# Revit family: Air_Handling_Unit-Package-Temperzone-OPA_171_211RLTFY
name_source: partatom
category: Mechanical Equipment
units: mm (PartAtom-declared; Revit-internal decimal feet)

## family parameters
Always vertical = Yes
Cut with Voids When Loaded = No
Maintain Annotation Orientation = No
OmniClass Number = 23.75.35.14
OmniClass Title = Air Handling Units
Part Type = Normal
Room Calculation Point = No
Round Connector Dimension = Use Radius
Shared = No
Work Plane-Based = No

## types (4) — shared parameters
Clearance Zones = Clearance Zones
ClearanceBack = 500 mm  [stored 1.64042 ft]
ClearanceLeft = 1000 mm  [stored 3.28084 ft]
ClearanceTop = 2000 mm
Condensate Drain = Condensate Drain - 1/2" BSP Female
CondensorFanBackOffset = 411 mm  [stored 1.34843 ft]
CondensorFanHeight = 18 mm  [stored 0.0590551 ft]
CondensorFanRadius = 290 mm  [stored 0.951444 ft]
Controller = UC8
DrainageBackOffset = 772 mm  [stored 2.53281 ft]
DrainageDia = 13 mm
DrainageLength = 30 mm  [stored 0.0984252 ft]
DrainageVerticalOffset = 83 mm  [stored 0.27231 ft]
ElectricInputVerticalOffset = 654 mm  [stored 2.14567 ft]
ElectricalRightOffset = 57 mm  [stored 0.187008 ft]
Finish = Grey Polyester Powder Coat
Indoor Fan Full Load Amps = 3 A/ph.
IndoorAirFanMotor = EC Motor
Manufacturer = temperzone ltd
ModifiedIssue_ANZRS = 250815.01 $
MountingFootHalfWidth = 64 mm
MountingFootLeftOffset = 24 mm  [stored 0.0787402 ft]
MountingPointLength = 800 mm  [stored 2.62467 ft]
NOTE = Models are representative of actual units, for exact model details please contact your Temperzone representative
OverallUnitHeight = 1176 mm  [stored 3.85827 ft]
Power Source = 3 phase 342-436V a.c. 50Hz
RASpigotDepth = 40 mm  [stored 0.131234 ft]
RASpigotVerticalOffset = 77 mm  [stored 0.252625 ft]
SASpigotHeight = 304 mm  [stored 0.997375 ft]
SASpigotVerticalOffset = 826 mm  [stored 2.70997 ft]
SpigotDepth = 40 mm  [stored 0.131234 ft]
Type Comments = The manufacturer reserves the right to change specifications at any time without notice or obligation. Certified dimensions available on request.
URL = www.temperzone.biz
UnitHeight = 1158 mm  [stored 3.79921 ft]
Voltage = 400 V
zero-valued in all types: Default Elevation

## per-type parameters (varying)
- OPA 171RLTFY(D)H: COP / ACOP_heating=3.42 / 3.38; CondensorFan1LeftOffset=697 mm  [stored 2.28675 ft]; CondensorFan2LeftOffset=697 mm  [stored 2.28675 ft]; DoubleCondensorFan=No; EER / AEER_cooling=3.34 / 3.30; HeatingCapacity_ANZRS=17300 W; Max Running Amps_Total=14 A/ph.; MountingFootLength=1224 mm; MountingFootWidth=127 mm; MountingPointWidth=1170 mm  [stored 3.83858 ft]; NetCoolingCapacity=16400 W; Nett Weight=250 kg; Nominal Airflow=900.0 L/s; NominalCoolingCapacity_ANZRS=16800 W; OverallUnitLength=1254 mm; OverallUnitWidth=1231 mm; RASpigotHeight=432 mm  [stored 1.41732 ft]; RASpigotLeftOffset=102 mm; RASpigotWidth=1030 mm  [stored 3.37927 ft]; Running Amps_Total System=9 / 7.5 / 9 A/ph.; SAPivotPlaneTopOffset=332 mm  [stored 1.08924 ft]; SASpigotAngle=0.00°; SASpigotLeftOffset=267 mm  [stored 0.875984 ft]; SASpigotWidth=778 mm  [stored 2.55249 ft]; Sound Power Level_at nominal airflow=75.6 dB(A); Sound Pressure Level_3m at nominal airflow=59.6 dB(A); UnitLength=1214 mm  [stored 3.98294 ft]; UnitWidth=1177 mm  [stored 3.86155 ft]
- OPA 211RLTFY(D)V: COP / ACOP_heating=3.67 / 3.63; CondensorFan1LeftOffset=505 mm  [stored 1.65682 ft]; CondensorFan2LeftOffset=1167 mm  [stored 3.82874 ft]; DoubleCondensorFan=Yes; EER / AEER_cooling=3.52 / 3.48; HeatingCapacity_ANZRS=19700 W; Max Running Amps_Total=20 A/ph.; MountingFootLength=1615 mm; MountingFootWidth=128 mm; MountingPointWidth=1571 mm; NetCoolingCapacity=19900 W; Nett Weight=298 kg; Nominal Airflow=1050.0 L/s; NominalCoolingCapacity_ANZRS=20300 W; OverallUnitLength=1256 mm; OverallUnitWidth=1621 mm; RASpigotHeight=534 mm  [stored 1.75197 ft]; RASpigotLeftOffset=104 mm; RASpigotWidth=1400 mm; Running Amps_Total System=10 / 8.5 / 11.5 A/ph.; SAPivotPlaneTopOffset=50 mm  [stored 0.164042 ft]; SASpigotAngle=90.00°; SASpigotLeftOffset=331 mm  [stored 1.08596 ft]; SASpigotWidth=905 mm  [stored 2.96916 ft]; Sound Power Level_at nominal airflow=78.6 dB(A); Sound Pressure Level_3m at nominal airflow=62.6 dB(A); UnitLength=1216 mm; UnitWidth=1567 mm
- OPA 211RLTFY(D)H: COP / ACOP_heating=3.67 / 3.63; CondensorFan1LeftOffset=505 mm  [stored 1.65682 ft]; CondensorFan2LeftOffset=1167 mm  [stored 3.82874 ft]; DoubleCondensorFan=Yes; EER / AEER_cooling=3.52 / 3.48; HeatingCapacity_ANZRS=19700 W; Max Running Amps_Total=20 A/ph.; MountingFootLength=1615 mm; MountingFootWidth=128 mm; MountingPointWidth=1571 mm; NetCoolingCapacity=19900 W; Nett Weight=298 kg; Nominal Airflow=1050.0 L/s; NominalCoolingCapacity_ANZRS=20300 W; OverallUnitLength=1256 mm; OverallUnitWidth=1621 mm; RASpigotHeight=534 mm  [stored 1.75197 ft]; RASpigotLeftOffset=104 mm; RASpigotWidth=1400 mm; Running Amps_Total System=10 / 8.5 / 11.5 A/ph.; SAPivotPlaneTopOffset=332 mm  [stored 1.08924 ft]; SASpigotAngle=0.00°; SASpigotLeftOffset=331 mm  [stored 1.08596 ft]; SASpigotWidth=905 mm  [stored 2.96916 ft]; Sound Power Level_at nominal airflow=78.6 dB(A); Sound Pressure Level_3m at nominal airflow=62.6 dB(A); UnitLength=1216 mm; UnitWidth=1567 mm
- OPA 171RLTFY(D)V: COP / ACOP_heating=3.42 / 3.38; CondensorFan1LeftOffset=697 mm  [stored 2.28675 ft]; CondensorFan2LeftOffset=697 mm  [stored 2.28675 ft]; DoubleCondensorFan=No; EER / AEER_cooling=3.34 / 3.30; HeatingCapacity_ANZRS=17300 W; Max Running Amps_Total=14 A/ph.; MountingFootLength=1224 mm; MountingFootWidth=127 mm; MountingPointWidth=1170 mm  [stored 3.83858 ft]; NetCoolingCapacity=16400 W; Nett Weight=250 kg; Nominal Airflow=900.0 L/s; NominalCoolingCapacity_ANZRS=16800 W; OverallUnitLength=1254 mm; OverallUnitWidth=1231 mm; RASpigotHeight=432 mm  [stored 1.41732 ft]; RASpigotLeftOffset=102 mm; RASpigotWidth=1030 mm  [stored 3.37927 ft]; Running Amps_Total System=9 / 7.5 / 9 A/ph.; SAPivotPlaneTopOffset=50 mm  [stored 0.164042 ft]; SASpigotAngle=90.00°; SASpigotLeftOffset=267 mm  [stored 0.875984 ft]; SASpigotWidth=778 mm  [stored 2.55249 ft]; Sound Power Level_at nominal airflow=75.6 dB(A); Sound Pressure Level_3m at nominal airflow=59.6 dB(A); UnitLength=1214 mm  [stored 3.98294 ft]; UnitWidth=1177 mm  [stored 3.86155 ft]

note: column(s) folded — value = type name in every type: Model

note: [stored X ft] marks values corroborated as IEEE doubles in the binary element streams (Revit-internal decimal feet)

## geometry (parser evidence)
native form markers: Sweep x2
no freeform markers — native parametric forms only
